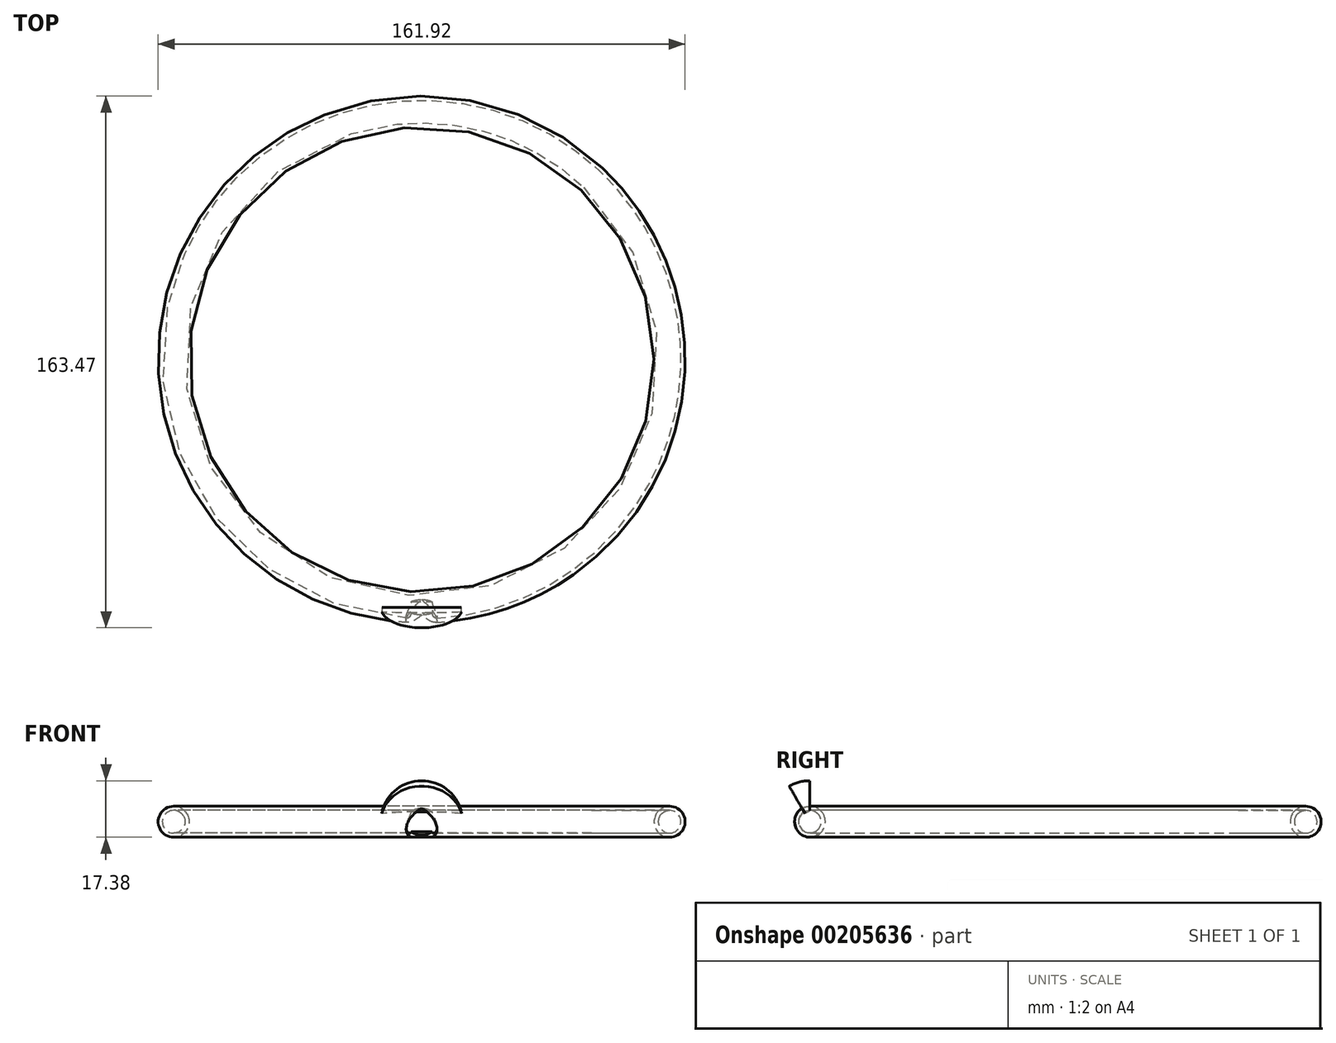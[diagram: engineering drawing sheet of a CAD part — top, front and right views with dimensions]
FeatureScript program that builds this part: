
annotation { "Feature Type Name" : "Feature", "Feature Type Description" : "" }
export const myFeature = defineFeature(function(context is Context, id is Id, definition is map)
    precondition{}
    {
        {
            var Q0;
            Q0=qCreatedBy(makeId("Front.planeOp"),FACE);
            var sketch = newSketch(context, id + "F0", { "sketchPlane" : qUnion([Q0])});
            skLineSegment(sketch, "E0", {"start": v(0, 0) * mm, "end": v(-76.2, 0) * mm, "construction": true});
            skCircle(sketch, "E1", {"center": v(-76.2, 0) * mm, "radius": 3.5 * mm});
            skCircle(sketch, "E2", {"center": v(-76.2, 0) * mm, "radius": 4.76 * mm});
            skLineSegment(sketch, "E3", {"start": v(0, 0) * mm, "end": v(0, 19.64) * mm, "construction": true});
            skSolve(sketch);
        }
        {
            var Q0;
            Q0 = qSketchRegion(id + "F0", true);
            var Q1;
            Q1=sQuery(id+"F0.wireOp",EDGE,"E3");
            revolve(context, id + "F1", {"entities" : qUnion([Q0]), "axis" : qUnion([Q1]), "revolveType" : RevolveType.FULL});
        }
        {
            var Q0;
            Q0=qCreatedBy(makeId("Front.planeOp"),FACE);
            cPlane(context, id + "F2", {"entities" : qUnion([Q0]), "cplaneType" : CPlaneType.OFFSET, "offset" : 76.2 * mm, "width" : 152.4 * mm, "height" : 152.4 * mm});
        }
        {
            var Q0;
            Q0=qCreatedBy(id+"F2.planeOp",FACE);
            var sketch = newSketch(context, id + "F3", { "sketchPlane" : qUnion([Q0])});
            skArc(sketch, "E4", {"start": v(-12.62, 0) * mm, "mid": v(0, 12.62) * mm, "end": v(12.62, 0) * mm});
            skLineSegment(sketch, "E5", {"start": v(-12.62, 0) * mm, "end": v(12.62, 0) * mm});
            skSolve(sketch);
        }
        {
            var Q0;
            Q0 = qSketchRegion(id + "F3", true);
            var Q1;
            Q1=sQuery(id+"F3.wireOp",EDGE,"E5");
            revolve(context, id + "F4", {"entities" : qUnion([Q0]), "axis" : qUnion([Q1]), "revolveType" : RevolveType.ONE_DIRECTION, "angle" : 30 * degree});
        }
        {
            var Q0;
            Q0=makeQuery(id+"F4.opRevolve","CAP_FACE",FACE,{"disambiguationData":[OSD([sQuery(id+"F3.wireOp",EDGE,"E4"),sQuery(id+"F3.wireOp",EDGE,"E5")])],"isStart":false});
            var sketch = newSketch(context, id + "F5", { "sketchPlane" : qUnion([Q0])});
            skCircle(sketch, "E6", {"center": v(0, 38.1) * mm, "radius": 3.5 * mm});
            skCircle(sketch, "E7", {"center": v(0, 38.1) * mm, "radius": 4.76 * mm});
            skSolve(sketch);
        }
        {
            var Q0;
            Q0 = qSketchRegion(id + "F5", true);
            extrude(context, id + "F6", {"entities" : qUnion([Q0]), "offsetDistance" : 25.4 * mm, "depth" : 25.4 * mm});
        }
        {
            var Q0;
            {var subQ0=sQuery(id+"F5.wireOp",EDGE,"E6");var subQ1=makeQuery(id+"F4.opRevolve","CAP_EDGE",EDGE,{"disambiguationData":[OSD([sQuery(id+"F3.wireOp",EDGE,"E5")])],"isStart":true});var subQ2=makeQuery(id+"F5.imprint","INTERSECT",VERTEX,{"disambiguationData":[OD(0.0)],"derivedFrom":[subQ1,subQ0]});Q0=makeQuery(id+"F5.imprint","IMPRINT",FACE,{"disambiguationData":[TD([[makeQuery(id+"F5.imprint","IMPRINT",EDGE,{"disambiguationData":[TD([[subQ2,-1.0]])],"derivedFrom":subQ0}),1.0]])]});}
            var Q1;
            {var subQ0=sQuery(id+"F5.wireOp",EDGE,"E6");var subQ1=makeQuery(id+"F4.opRevolve","CAP_EDGE",EDGE,{"disambiguationData":[OSD([sQuery(id+"F3.wireOp",EDGE,"E5")])],"isStart":true});var subQ2=makeQuery(id+"F5.imprint","INTERSECT",VERTEX,{"disambiguationData":[OD(0.0)],"derivedFrom":[subQ1,subQ0]});Q1=makeQuery(id+"F5.imprint","IMPRINT",FACE,{"disambiguationData":[TD([[makeQuery(id+"F5.imprint","IMPRINT",EDGE,{"disambiguationData":[TD([[subQ2,1.0]])],"derivedFrom":subQ0}),1.0]])]});}
            var Q2;
            {var subQ0=sQuery(id+"F5.wireOp",EDGE,"E6");var subQ1=makeQuery(id+"F4.opRevolve","CAP_EDGE",EDGE,{"disambiguationData":[OSD([sQuery(id+"F3.wireOp",EDGE,"E5")])],"isStart":true});var subQ2=makeQuery(id+"F5.imprint","INTERSECT",VERTEX,{"disambiguationData":[OD(0.0)],"derivedFrom":[subQ1,subQ0]});Q2=makeQuery(id+"F5.imprint","IMPRINT",FACE,{"disambiguationData":[TD([[makeQuery(id+"F5.imprint","IMPRINT",EDGE,{"disambiguationData":[TD([[subQ2,-1.0]])],"derivedFrom":subQ0}),-1.0]])]});}
            var Q3;
            {var subQ0=sQuery(id+"F5.wireOp",EDGE,"E6");var subQ1=makeQuery(id+"F4.opRevolve","CAP_EDGE",EDGE,{"disambiguationData":[OSD([sQuery(id+"F3.wireOp",EDGE,"E5")])],"isStart":true});var subQ2=makeQuery(id+"F5.imprint","INTERSECT",VERTEX,{"disambiguationData":[OD(0.0)],"derivedFrom":[subQ1,subQ0]});Q3=makeQuery(id+"F5.imprint","IMPRINT",FACE,{"disambiguationData":[TD([[makeQuery(id+"F5.imprint","IMPRINT",EDGE,{"disambiguationData":[TD([[subQ2,1.0]])],"derivedFrom":subQ0}),-1.0]])]});}
            extrude(context, id + "F7", {"entities" : qUnion([Q0, Q1, Q2, Q3]), "operationType" : NewBodyOperationType.REMOVE, "depth" : 25.4 * mm});
        }
        {
            var Q0;
            Q0=makeQuery(id+"F0.imprint","IMPRINT",FACE,{"disambiguationData":[TD([[makeQuery(id+"F0.imprint","IMPRINT",EDGE,{"derivedFrom":sQuery(id+"F0.wireOp",EDGE,"E1")}),1.0]])]});
            var Q1;
            Q1=sQuery(id+"F0.wireOp",EDGE,"E3");
            revolve(context, id + "F8", {"operationType" : NewBodyOperationType.REMOVE, "entities" : qUnion([Q0]), "axis" : qUnion([Q1]), "revolveType" : RevolveType.FULL, "oppositeDirection" : true});
        }
    });
